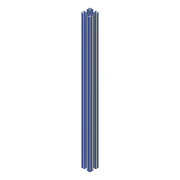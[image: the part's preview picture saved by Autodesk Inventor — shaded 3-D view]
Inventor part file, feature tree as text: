
AUTODESK INVENTOR PART (.ipt)
format: ipt  version: 2018.1 (Build 221171000, 171)  size: 227,328 bytes
history: native  units: mm
features: other x2, extrude x1
ambient origin geometry x8: Origin, YZ Plane, XZ Plane, XY Plane, X Axis, Y Axis, Z Axis, Center Point
bodies: Volumenkörper1 (feature_tree)
feature tree (3):
  other  "Vorlage_Aluprofile_30x30.ipt"
  extrude  "Extrusion1"  Depth=10.0mm
  other  "Profil_Skizze"
